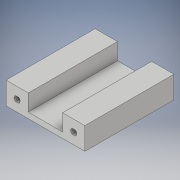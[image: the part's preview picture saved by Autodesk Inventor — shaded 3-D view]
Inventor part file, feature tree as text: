
AUTODESK INVENTOR PART (.ipt)
format: ipt  version: 2019 (Build 230136000, 136)  size: 117,760 bytes
history: native  units: in
note: dims shown in document units (in); Inventor stores cm internally (conversion verified against a paired STEP export)
features: sketch x2, extrude x1
ambient origin geometry x8: Origin, YZ Plane, XZ Plane, XY Plane, X Axis, Y Axis, Z Axis, Center Point
bodies: Solid1 (feature_tree)
feature tree (3):
  sketch  "Sketch1"  dims[d0=0.7874in d2=0.2098in d3=0.2098in]
  extrude  "Extrusion1"  Depth=0.7874in
  sketch  "Sketch2"  dims[d5=0.394in d9=0.1787in d10=0.8027in d11=0.8027in d12=0.1787in d13=0.8027in d14=0.8027in d15=0.3937in d16=2.0in d17=0.2in d18=0.3937in d19=3.1496in d20=0.0in]
